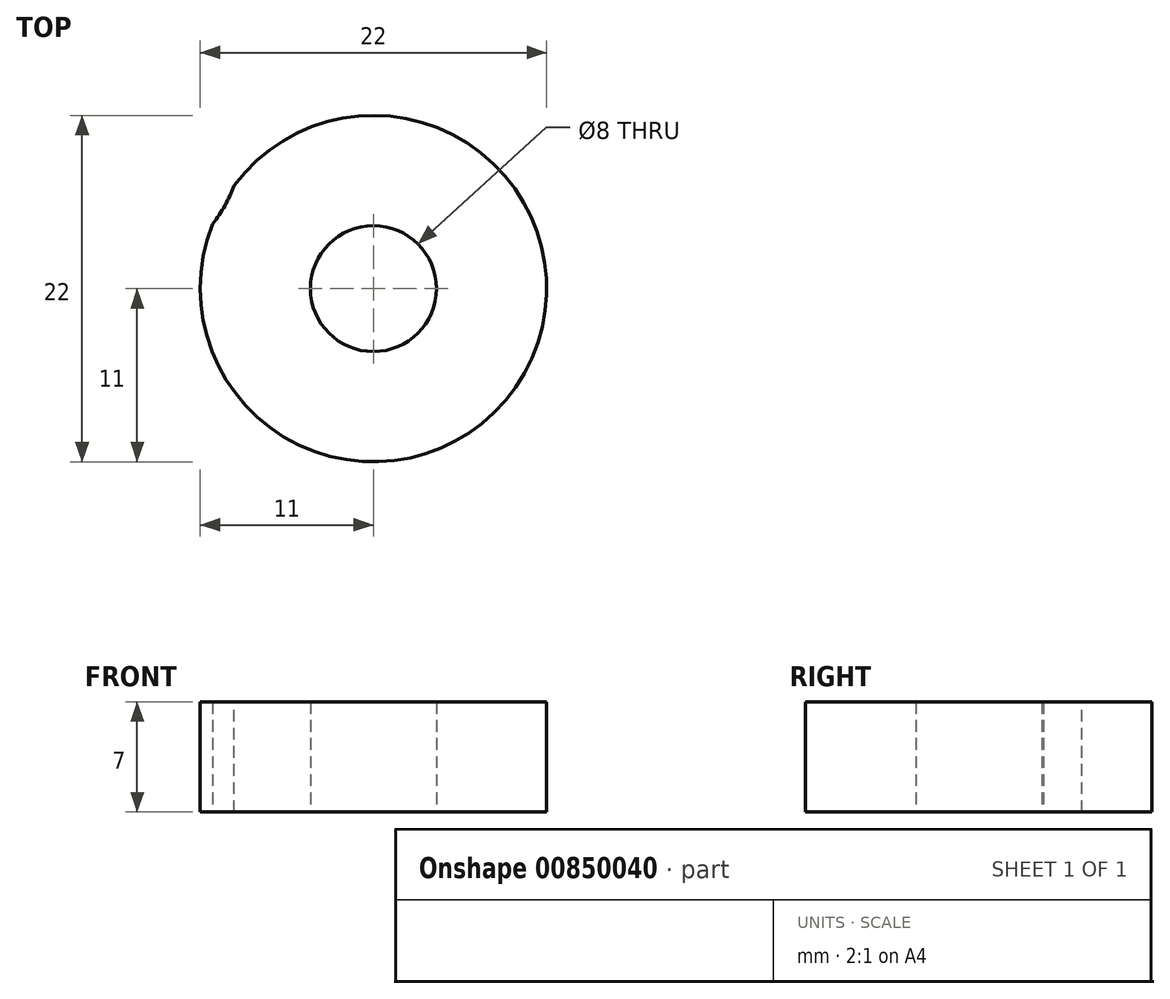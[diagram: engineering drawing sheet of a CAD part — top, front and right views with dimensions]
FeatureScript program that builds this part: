
annotation { "Feature Type Name" : "Feature", "Feature Type Description" : "" }
export const myFeature = defineFeature(function(context is Context, id is Id, definition is map)
    precondition{}
    {
        {
            var Q0;
            Q0=qCreatedBy(makeId("Top.planeOp"),FACE);
            var sketch = newSketch(context, id + "F0", { "sketchPlane" : qUnion([Q0])});
            skCircle(sketch, "E0", {"center": v(0, 34.39) * mm, "radius": 10 * mm});
            skCircle(sketch, "E1.0", {"center": v(0, 34.39) * mm, "radius": 15 * mm});
            skCircle(sketch, "E2", {"center": v(0, 0) * mm, "radius": 4 * mm});
            skCircle(sketch, "E3", {"center": v(0, 0) * mm, "radius": 11 * mm});
            skCircle(sketch, "E4.1.0", {"center": v(-34.57, -22.07) * mm, "radius": 10 * mm});
            skCircle(sketch, "E4.1.1", {"center": v(-34.57, -22.07) * mm, "radius": 15 * mm});
            skCircle(sketch, "E4.2.0", {"center": v(31.6, -23.78) * mm, "radius": 10 * mm});
            skCircle(sketch, "E4.2.1", {"center": v(31.6, -23.78) * mm, "radius": 15 * mm});
            skPoint(sketch, "E4.center", {"position": v(-0.99, -3.82) * mm});
            skLineSegment(sketch, "E5", {"start": v(0, 0) * mm, "end": v(-24.57, 50.7) * mm, "construction": true});
            skLineSegment(sketch, "E6", {"start": v(0, 0) * mm, "end": v(-56.06, -11) * mm, "construction": true});
            skLineSegment(sketch, "E7", {"start": v(-37.46, -7.35) * mm, "end": v(-13.5, 27.84) * mm, "construction": true});
            skLineSegment(sketch, "E8", {"start": v(0, 0) * mm, "end": v(-25.48, 10.25) * mm, "construction": true});
            skFitSpline(sketch, "E9", {"points": [v(-13.5, 27.84) * mm, v(-10.2, 4.1) * mm, v(-37.46, -7.35) * mm], "startDerivative": vector(36.49, -75.27) * mm, "endDerivative": vector(-74.47, -18.8) * mm});
            skLineSegment(sketch, "E10.1.0", {"start": v(0, 0) * mm, "end": v(-31.61, -46.63) * mm, "construction": true});
            skLineSegment(sketch, "E10.1.1", {"start": v(25.1, -28.77) * mm, "end": v(-17.36, -25.61) * mm, "construction": true});
            skLineSegment(sketch, "E10.1.2", {"start": v(0, 0) * mm, "end": v(3.87, -27.19) * mm, "construction": true});
            skLineSegment(sketch, "E10.1.3", {"start": v(0, 0) * mm, "end": v(37.56, -43.05) * mm, "construction": true});
            skLineSegment(sketch, "E10.2.0", {"start": v(0, 0) * mm, "end": v(56.19, -4.06) * mm, "construction": true});
            skLineSegment(sketch, "E10.2.1", {"start": v(12.36, 36.12) * mm, "end": v(30.86, -2.23) * mm, "construction": true});
            skLineSegment(sketch, "E10.2.2", {"start": v(0, 0) * mm, "end": v(21.61, 16.94) * mm, "construction": true});
            skLineSegment(sketch, "E10.2.3", {"start": v(0, 0) * mm, "end": v(18.5, 54.05) * mm, "construction": true});
            skSolve(sketch);
        }
        {
            var Q0;
            Q0=makeQuery(id+"F0.imprint","IMPRINT",FACE,{"disambiguationData":[TD([[makeQuery(id+"F0.imprint","IMPRINT",EDGE,{"derivedFrom":sQuery(id+"F0.wireOp",EDGE,"E2")}),-1.0]])]});
            extrude(context, id + "F1", {"entities" : qUnion([Q0]), "endBound" : BoundingType.SYMMETRIC, "depth" : 7 * mm, "offsetDistance" : 25 * mm});
        }
    });
